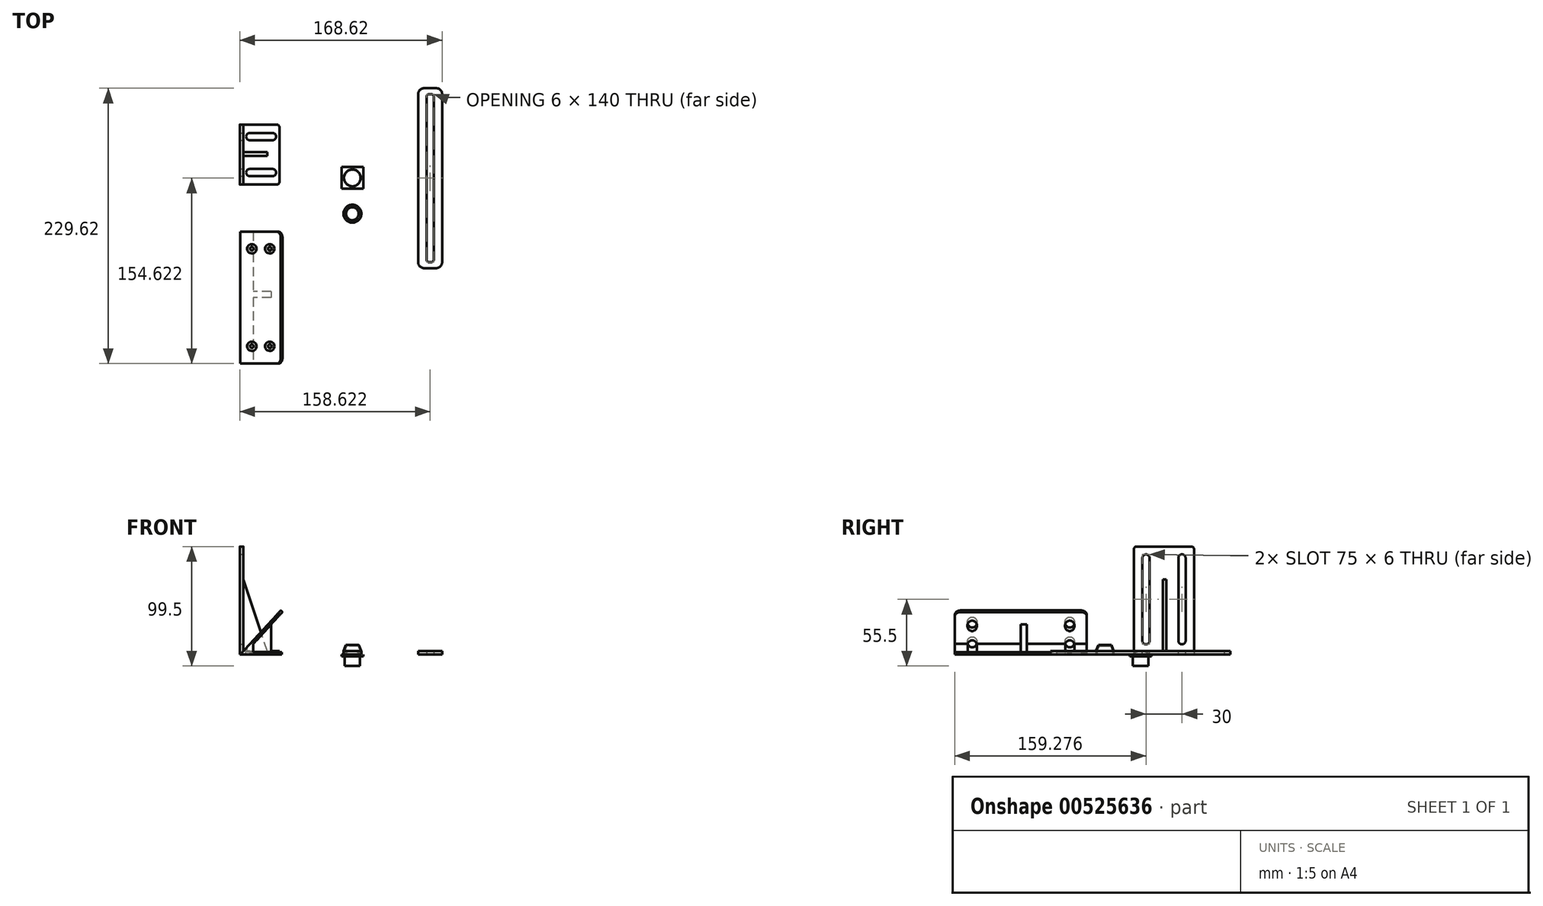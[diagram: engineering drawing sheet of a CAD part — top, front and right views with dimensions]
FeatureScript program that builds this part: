
annotation { "Feature Type Name" : "Feature", "Feature Type Description" : "" }
export const myFeature = defineFeature(function(context is Context, id is Id, definition is map)
    precondition{}
    {
        {
            var Q0;
            Q0=qCreatedBy(makeId("Top.planeOp"),FACE);
            var sketch = newSketch(context, id + "F0", { "sketchPlane" : qUnion([Q0])});
            skCircle(sketch, "E0", {"center": v(0, 0) * mm, "radius": 7 * mm});
            skSolve(sketch);
        }
        {
            var Q0;
            Q0=makeQuery(id+"F0.imprint","IMPRINT",FACE,{"disambiguationData":[TD([[makeQuery(id+"F0.imprint","IMPRINT",EDGE,{"derivedFrom":sQuery(id+"F0.wireOp",EDGE,"E0")}),1.0]])]});
            extrude(context, id + "F1", {"entities" : qUnion([Q0]), "depth" : 2.5 * mm, "offsetDistance" : 25 * mm});
        }
        {
            var Q0;
            Q0=makeQuery(id+"F1.opExtrude","CAP_EDGE",EDGE,{"disambiguationData":[OSD([sQuery(id+"F0.wireOp",EDGE,"E0")])],"isStart":false});
            fillet(context, id + "F2", {"entities" : qUnion([Q0]), "radius" : 7 * mm, "tangentPropagation" : true, "allowEdgeOverflow" : false});
        }
        {
            var Q0;
            Q0=makeQuery(id+"F1.opExtrude","CAP_FACE",FACE,{"disambiguationData":[OSD([sQuery(id+"F0.wireOp",EDGE,"E0")])],"isStart":true});
            cPlane(context, id + "F3", {"entities" : qUnion([Q0]), "cplaneType" : CPlaneType.OFFSET, "offset" : 0 * mm, "width" : 150 * mm, "height" : 150 * mm});
        }
        {
            var Q0;
            Q0=qCreatedBy(id+"F3.planeOp",FACE);
            var sketch = newSketch(context, id + "F4", { "sketchPlane" : qUnion([Q0])});
            skLineSegment(sketch, "E1.bottom", {"start": v(-9, -9) * mm, "end": v(9, -9) * mm});
            skLineSegment(sketch, "E1.top", {"start": v(-9, 9) * mm, "end": v(9, 9) * mm});
            skLineSegment(sketch, "E1.left", {"start": v(-9, -9) * mm, "end": v(-9, 9) * mm});
            skLineSegment(sketch, "E1.right", {"start": v(9, -9) * mm, "end": v(9, 9) * mm});
            skSolve(sketch);
        }
        {
            var Q0;
            Q0=qSketchRegion(id+"F4",true);
            extrude(context, id + "F5", {"entities" : qUnion([Q0]), "operationType" : NewBodyOperationType.ADD, "depth" : 1.5 * mm, "offsetDistance" : 25 * mm});
        }
        {
            var Q0;
            Q0=makeQuery(id+"F5.opExtrude","CAP_FACE",FACE,{"disambiguationData":[OSD([sQuery(id+"F4.wireOp",EDGE,"E1.bottom"),sQuery(id+"F4.wireOp",EDGE,"E1.top"),sQuery(id+"F4.wireOp",EDGE,"E1.left"),sQuery(id+"F4.wireOp",EDGE,"E1.right")])],"isStart":false});
            cPlane(context, id + "F6", {"entities" : qUnion([Q0]), "cplaneType" : CPlaneType.OFFSET, "offset" : 0 * mm, "width" : 150 * mm, "height" : 150 * mm});
        }
        {
            var Q0;
            Q0=qCreatedBy(id+"F6.planeOp",FACE);
            var sketch = newSketch(context, id + "F7", { "sketchPlane" : qUnion([Q0])});
            skCircle(sketch, "E2", {"center": v(0, 0) * mm, "radius": 6.4 * mm});
            skSolve(sketch);
        }
        {
            var Q0;
            Q0=qSketchRegion(id+"F7",true);
            extrude(context, id + "F8", {"entities" : qUnion([Q0]), "operationType" : NewBodyOperationType.ADD, "depth" : 8 * mm, "offsetDistance" : 25 * mm});
        }
        {
            var Q0;
            Q0=qCreatedBy(makeId("Top.planeOp"),FACE);
            var sketch = newSketch(context, id + "F9", { "sketchPlane" : qUnion([Q0])});
            skCircle(sketch, "E3", {"center": v(0, -29.84) * mm, "radius": 7.45 * mm});
            skSolve(sketch);
        }
        {
            var Q0;
            Q0=qSketchRegion(id+"F9",true);
            extrude(context, id + "F10", {"entities" : qUnion([Q0]), "depth" : 8 * mm, "offsetDistance" : 25 * mm});
        }
        {
            var Q0;
            Q0=makeQuery(id+"F10.opExtrude","CAP_EDGE",EDGE,{"disambiguationData":[OSD([sQuery(id+"F9.wireOp",EDGE,"E3")])],"isStart":false});
            chamfer(context, id + "F11", {"entities" : qUnion([Q0]), "chamferType" : ChamferType.TWO_OFFSETS, "width1" : 2 * mm, "oppositeDirection" : false, "width2" : 5 * mm, "tangentPropagation" : true});
        }
        {
            var Q0;
            Q0=qCreatedBy(makeId("Top.planeOp"),FACE);
            var sketch = newSketch(context, id + "F12", { "sketchPlane" : qUnion([Q0])});
            skCircle(sketch, "E4", {"center": v(0, -29.84) * mm, "radius": 6.45 * mm});
            skSolve(sketch);
        }
        {
            var Q0;
            Q0=qSketchRegion(id+"F12",true);
            extrude(context, id + "F13", {"entities" : qUnion([Q0]), "depth" : 7 * mm, "offsetDistance" : 25 * mm});
        }
        {
            var Q0;
            Q0=makeQuery(id+"F13.opExtrude","CAP_EDGE",EDGE,{"disambiguationData":[OSD([sQuery(id+"F12.wireOp",EDGE,"E4")])],"isStart":false});
            chamfer(context, id + "F14", {"entities" : qUnion([Q0]), "chamferType" : ChamferType.TWO_OFFSETS, "width1" : 1.7 * mm, "oppositeDirection" : false, "width2" : 4 * mm, "tangentPropagation" : true});
        }
        {
            var Q0;
            Q0=makeQuery(id+"F13.opExtrude","SWEPT_BODY",BODY,{"disambiguationData":[OSD([sQuery(id+"F12.wireOp",EDGE,"E4")])]});
            var Q1;
            Q1=makeQuery(id+"F10.opExtrude","SWEPT_BODY",BODY,{"disambiguationData":[OSD([sQuery(id+"F9.wireOp",EDGE,"E3")])]});
            booleanBodies(context, id + "F15", {"operationType" : BooleanOperationType.SUBTRACTION, "tools" : qUnion([Q0]), "targets" : qUnion([Q1])});
        }
        {
            var Q0;
            Q0=qCreatedBy(makeId("Top.planeOp"),FACE);
            var sketch = newSketch(context, id + "F16", { "sketchPlane" : qUnion([Q0])});
            skLineSegment(sketch, "E5.bottom", {"start": v(59.8, 74.78) * mm, "end": v(69.8, 74.78) * mm});
            skLineSegment(sketch, "E5.top", {"start": v(59.8, -75.22) * mm, "end": v(69.8, -75.22) * mm});
            skLineSegment(sketch, "E5.left", {"start": v(54.8, 69.78) * mm, "end": v(54.8, -70.22) * mm});
            skLineSegment(sketch, "E5.right", {"start": v(74.8, 69.78) * mm, "end": v(74.8, -70.22) * mm});
            skPoint(sketch, "E6.visualSharp", {"position": v(54.8, 74.78) * mm});
            skArc(sketch, "E6.filletArc", {"start": v(59.8, 74.78) * mm, "mid": v(56.27, 73.32) * mm, "end": v(54.8, 69.78) * mm});
            skPoint(sketch, "E7.visualSharp", {"position": v(74.8, 74.78) * mm});
            skArc(sketch, "E7.filletArc", {"start": v(74.8, 69.78) * mm, "mid": v(73.34, 73.32) * mm, "end": v(69.8, 74.78) * mm});
            skPoint(sketch, "E8.visualSharp", {"position": v(54.8, -75.22) * mm});
            skArc(sketch, "E8.filletArc", {"start": v(54.8, -70.22) * mm, "mid": v(56.27, -73.75) * mm, "end": v(59.8, -75.22) * mm});
            skPoint(sketch, "E9.visualSharp", {"position": v(74.8, -75.22) * mm});
            skArc(sketch, "E9.filletArc", {"start": v(69.8, -75.22) * mm, "mid": v(73.34, -73.75) * mm, "end": v(74.8, -70.22) * mm});
            skLineSegment(sketch, "E10.bottom", {"start": v(63.8, 69.78) * mm, "end": v(65.8, 69.78) * mm});
            skLineSegment(sketch, "E10.top", {"start": v(63.8, -70.22) * mm, "end": v(65.8, -70.22) * mm});
            skLineSegment(sketch, "E10.left", {"start": v(61.8, 67.78) * mm, "end": v(61.8, -68.22) * mm});
            skLineSegment(sketch, "E10.right", {"start": v(67.8, 67.78) * mm, "end": v(67.8, -68.22) * mm});
            skPoint(sketch, "E11.visualSharp", {"position": v(61.8, 69.78) * mm});
            skArc(sketch, "E11.filletArc", {"start": v(63.8, 69.78) * mm, "mid": v(62.39, 69.2) * mm, "end": v(61.8, 67.78) * mm});
            skPoint(sketch, "E12.visualSharp", {"position": v(61.8, -70.22) * mm});
            skArc(sketch, "E12.filletArc", {"start": v(61.8, -68.22) * mm, "mid": v(62.39, -69.63) * mm, "end": v(63.8, -70.22) * mm});
            skPoint(sketch, "E13.visualSharp", {"position": v(67.8, -70.22) * mm});
            skArc(sketch, "E13.filletArc", {"start": v(65.8, -70.22) * mm, "mid": v(67.22, -69.63) * mm, "end": v(67.8, -68.22) * mm});
            skPoint(sketch, "E14.visualSharp", {"position": v(67.8, 69.78) * mm});
            skArc(sketch, "E14.filletArc", {"start": v(67.8, 67.78) * mm, "mid": v(67.22, 69.2) * mm, "end": v(65.8, 69.78) * mm});
            skSolve(sketch);
        }
        {
            var Q0;
            Q0=qSketchRegion(id+"F16",true);
            extrude(context, id + "F17", {"entities" : qUnion([Q0]), "depth" : 3 * mm, "offsetDistance" : 25 * mm});
        }
        {
            var Q0;
            Q0=qCreatedBy(makeId("Top.planeOp"),FACE);
            var sketch = newSketch(context, id + "F18", { "sketchPlane" : qUnion([Q0])});
            skLineSegment(sketch, "E15.bottom", {"start": v(-90.82, 44.44) * mm, "end": v(-62.82, 44.44) * mm});
            skLineSegment(sketch, "E15.top", {"start": v(-90.82, -5.56) * mm, "end": v(-62.82, -5.56) * mm});
            skLineSegment(sketch, "E15.left", {"start": v(-90.82, 44.44) * mm, "end": v(-90.82, -5.56) * mm});
            skLineSegment(sketch, "E15.right", {"start": v(-60.82, 42.44) * mm, "end": v(-60.82, -3.56) * mm});
            skPoint(sketch, "E16.visualSharp", {"position": v(-60.82, 44.44) * mm});
            skArc(sketch, "E16.filletArc", {"start": v(-60.82, 42.44) * mm, "mid": v(-61.4, 43.85) * mm, "end": v(-62.82, 44.44) * mm});
            skPoint(sketch, "E17.visualSharp", {"position": v(-60.82, -5.56) * mm});
            skArc(sketch, "E17.filletArc", {"start": v(-62.82, -5.56) * mm, "mid": v(-61.4, -4.98) * mm, "end": v(-60.82, -3.56) * mm});
            skLineSegment(sketch, "E18.bottom", {"start": v(-101.44, 55.6) * mm, "end": v(-90.82, 55.6) * mm, "construction": true});
            skLineSegment(sketch, "E18.top", {"start": v(-101.44, -19.09) * mm, "end": v(-90.82, -19.09) * mm, "construction": true});
            skLineSegment(sketch, "E18.left", {"start": v(-101.44, 55.6) * mm, "end": v(-101.44, -19.09) * mm, "construction": true});
            skLineSegment(sketch, "E18.right", {"start": v(-90.82, 55.6) * mm, "end": v(-90.82, -19.09) * mm, "construction": true});
            skSolve(sketch);
        }
        {
            var Q0;
            Q0=qSketchRegion(id+"F18",true);
            extrude(context, id + "F19", {"entities" : qUnion([Q0]), "depth" : 3 * mm, "offsetDistance" : 25 * mm});
        }
        {
            var Q0;
            Q0=qCreatedBy(makeId("Top.planeOp"),FACE);
            var sketch = newSketch(context, id + "F20", { "sketchPlane" : qUnion([Q0])});
            skLineSegment(sketch, "E19.bottom", {"start": v(-93.82, 44.44) * mm, "end": v(-90.82, 44.44) * mm});
            skLineSegment(sketch, "E19.top", {"start": v(-93.82, -5.56) * mm, "end": v(-90.82, -5.56) * mm});
            skLineSegment(sketch, "E19.left", {"start": v(-93.82, 44.44) * mm, "end": v(-93.82, -5.56) * mm});
            skLineSegment(sketch, "E19.right", {"start": v(-90.82, 44.44) * mm, "end": v(-90.82, -5.56) * mm});
            skSolve(sketch);
        }
        {
            var Q0;
            Q0=qSketchRegion(id+"F20",true);
            extrude(context, id + "F21", {"entities" : qUnion([Q0]), "operationType" : NewBodyOperationType.ADD, "depth" : 90 * mm, "offsetDistance" : 25 * mm});
        }
        {
            var Q0;
            Q0=makeQuery(id+"F21.opExtrude","CAP_EDGE",EDGE,{"disambiguationData":[OSD([sQuery(id+"F20.wireOp",EDGE,"E19.top")])],"isStart":false});
            var Q1;
            Q1=makeQuery(id+"F21.opExtrude","CAP_EDGE",EDGE,{"disambiguationData":[OSD([sQuery(id+"F20.wireOp",EDGE,"E19.bottom")])],"isStart":false});
            fillet(context, id + "F22", {"entities" : qUnion([Q0, Q1]), "radius" : 2 * mm, "tangentPropagation" : true, "allowEdgeOverflow" : false});
        }
        {
            var Q0;
            Q0=makeQuery(id+"F19.opExtrude","CAP_FACE",FACE,{"disambiguationData":[OSD([sQuery(id+"F18.wireOp",EDGE,"E15.bottom"),sQuery(id+"F18.wireOp",EDGE,"E15.top"),sQuery(id+"F18.wireOp",EDGE,"E15.left"),sQuery(id+"F18.wireOp",EDGE,"E15.right"),sQuery(id+"F18.wireOp",EDGE,"E16.filletArc"),sQuery(id+"F18.wireOp",EDGE,"E17.filletArc")])],"isStart":false});
            var sketch = newSketch(context, id + "F23", { "sketchPlane" : qUnion([Q0])});
            skLineSegment(sketch, "E20.bottom", {"start": v(-85.49, 37.44) * mm, "end": v(-66.49, 37.44) * mm});
            skLineSegment(sketch, "E20.top", {"start": v(-85.49, 31.44) * mm, "end": v(-66.49, 31.44) * mm});
            skLineSegment(sketch, "E20.left", {"start": v(-88.49, 34.44) * mm, "end": v(-88.49, 34.44) * mm});
            skLineSegment(sketch, "E20.right", {"start": v(-63.49, 34.44) * mm, "end": v(-63.49, 34.44) * mm});
            skPoint(sketch, "E21.visualSharp", {"position": v(-88.49, 37.44) * mm});
            skArc(sketch, "E21.filletArc", {"start": v(-85.49, 37.44) * mm, "mid": v(-87.6, 36.56) * mm, "end": v(-88.49, 34.44) * mm});
            skPoint(sketch, "E22.visualSharp", {"position": v(-88.49, 31.44) * mm});
            skArc(sketch, "E22.filletArc", {"start": v(-88.49, 34.44) * mm, "mid": v(-87.6, 32.31) * mm, "end": v(-85.49, 31.44) * mm});
            skPoint(sketch, "E23.visualSharp", {"position": v(-63.49, 31.44) * mm});
            skArc(sketch, "E23.filletArc", {"start": v(-66.49, 31.44) * mm, "mid": v(-64.37, 32.31) * mm, "end": v(-63.49, 34.44) * mm});
            skPoint(sketch, "E24.visualSharp", {"position": v(-63.49, 37.44) * mm});
            skArc(sketch, "E24.filletArc", {"start": v(-63.49, 34.44) * mm, "mid": v(-64.37, 36.56) * mm, "end": v(-66.49, 37.44) * mm});
            skLineSegment(sketch, "E25.bottom", {"start": v(-85.49, 7.44) * mm, "end": v(-66.49, 7.44) * mm});
            skLineSegment(sketch, "E25.top", {"start": v(-85.49, 1.44) * mm, "end": v(-66.49, 1.44) * mm});
            skLineSegment(sketch, "E25.left", {"start": v(-88.49, 4.44) * mm, "end": v(-88.49, 4.44) * mm});
            skLineSegment(sketch, "E25.right", {"start": v(-63.49, 4.44) * mm, "end": v(-63.49, 4.44) * mm});
            skPoint(sketch, "E26.visualSharp", {"position": v(-88.49, 7.44) * mm});
            skArc(sketch, "E26.filletArc", {"start": v(-85.49, 7.44) * mm, "mid": v(-87.61, 6.56) * mm, "end": v(-88.49, 4.44) * mm});
            skPoint(sketch, "E27.visualSharp", {"position": v(-88.49, 1.44) * mm});
            skArc(sketch, "E27.filletArc", {"start": v(-88.49, 4.44) * mm, "mid": v(-87.61, 2.31) * mm, "end": v(-85.49, 1.44) * mm});
            skPoint(sketch, "E28.visualSharp", {"position": v(-63.49, 1.44) * mm});
            skArc(sketch, "E28.filletArc", {"start": v(-66.49, 1.44) * mm, "mid": v(-64.37, 2.31) * mm, "end": v(-63.49, 4.44) * mm});
            skPoint(sketch, "E29.visualSharp", {"position": v(-63.49, 7.44) * mm});
            skArc(sketch, "E29.filletArc", {"start": v(-63.49, 4.44) * mm, "mid": v(-64.37, 6.56) * mm, "end": v(-66.49, 7.44) * mm});
            skSolve(sketch);
        }
        {
            var Q0;
            Q0=qSketchRegion(id+"F23",true);
            extrude(context, id + "F24", {"entities" : qUnion([Q0]), "operationType" : NewBodyOperationType.REMOVE, "oppositeDirection" : true, "depth" : 25 * mm, "offsetDistance" : 25 * mm});
        }
        {
            var Q0;
            Q0=makeQuery(id+"F21.opExtrude","SWEPT_FACE",FACE,{"disambiguationData":[OSD([sQuery(id+"F20.wireOp",EDGE,"E19.right")])]});
            var sketch = newSketch(context, id + "F25", { "sketchPlane" : qUnion([Q0])});
            skLineSegment(sketch, "E30.bottom", {"start": v(34.44, 83.5) * mm, "end": v(34.44, 83.5) * mm});
            skLineSegment(sketch, "E30.top", {"start": v(34.44, 8.5) * mm, "end": v(34.44, 8.5) * mm});
            skLineSegment(sketch, "E30.left", {"start": v(31.44, 80.5) * mm, "end": v(31.44, 11.5) * mm});
            skLineSegment(sketch, "E30.right", {"start": v(37.44, 80.5) * mm, "end": v(37.44, 11.5) * mm});
            skPoint(sketch, "E31.visualSharp", {"position": v(31.44, 83.5) * mm});
            skArc(sketch, "E31.filletArc", {"start": v(34.44, 83.5) * mm, "mid": v(32.31, 82.62) * mm, "end": v(31.44, 80.5) * mm});
            skPoint(sketch, "E32.visualSharp", {"position": v(31.44, 8.5) * mm});
            skArc(sketch, "E32.filletArc", {"start": v(31.44, 11.5) * mm, "mid": v(32.31, 9.38) * mm, "end": v(34.44, 8.5) * mm});
            skPoint(sketch, "E33.visualSharp", {"position": v(37.44, 83.5) * mm});
            skArc(sketch, "E33.filletArc", {"start": v(37.44, 80.5) * mm, "mid": v(36.56, 82.62) * mm, "end": v(34.44, 83.5) * mm});
            skPoint(sketch, "E34.visualSharp", {"position": v(37.44, 8.5) * mm});
            skArc(sketch, "E34.filletArc", {"start": v(34.44, 8.5) * mm, "mid": v(36.56, 9.38) * mm, "end": v(37.44, 11.5) * mm});
            skLineSegment(sketch, "E35.bottom", {"start": v(49.07, 61.34) * mm, "end": v(49.07, 61.34) * mm});
            skLineSegment(sketch, "E35.top", {"start": v(49.07, -13.66) * mm, "end": v(49.07, -13.66) * mm});
            skLineSegment(sketch, "E35.left", {"start": v(1.44, 80.5) * mm, "end": v(1.44, 11.5) * mm});
            skLineSegment(sketch, "E35.right", {"start": v(7.44, 80.5) * mm, "end": v(7.44, 11.5) * mm});
            skPoint(sketch, "E36.visualSharp", {"position": v(1.44, 83.5) * mm});
            skArc(sketch, "E36.filletArc", {"start": v(4.44, 83.5) * mm, "mid": v(2.31, 82.62) * mm, "end": v(1.44, 80.5) * mm});
            skPoint(sketch, "E37.visualSharp", {"position": v(1.44, 8.5) * mm});
            skArc(sketch, "E37.filletArc", {"start": v(1.44, 11.5) * mm, "mid": v(2.31, 9.38) * mm, "end": v(4.44, 8.5) * mm});
            skPoint(sketch, "E38.visualSharp", {"position": v(7.44, 83.5) * mm});
            skArc(sketch, "E38.filletArc", {"start": v(7.44, 80.5) * mm, "mid": v(6.56, 82.62) * mm, "end": v(4.44, 83.5) * mm});
            skPoint(sketch, "E39.visualSharp", {"position": v(7.44, 8.5) * mm});
            skArc(sketch, "E39.filletArc", {"start": v(4.44, 8.5) * mm, "mid": v(6.56, 9.38) * mm, "end": v(7.44, 11.5) * mm});
            skSolve(sketch);
        }
        {
            var Q0;
            Q0=qSketchRegion(id+"F25",true);
            extrude(context, id + "F26", {"entities" : qUnion([Q0]), "operationType" : NewBodyOperationType.REMOVE, "oppositeDirection" : true, "depth" : 25 * mm, "offsetDistance" : 25 * mm});
        }
        {
            var Q0;
            Q0=makeQuery(id+"F29.boolean.opBoolean","MERGE",FACE,{"derivedFrom":[makeQuery(id+"F21.boolean.opBoolean","MERGE",FACE,{"derivedFrom":[makeQuery(id+"F19.opExtrude","SWEPT_FACE",FACE,{"disambiguationData":[OSD([sQuery(id+"F18.wireOp",EDGE,"E15.top")])]}),makeQuery(id+"F21.opExtrude","SWEPT_FACE",FACE,{"disambiguationData":[OSD([sQuery(id+"F20.wireOp",EDGE,"E19.top")])]})]}),makeQuery(id+"F29.opExtrude","CAP_FACE",FACE,{"disambiguationData":[OSD([sQuery(id+"F28.wireOp",EDGE,"E40"),sQuery(id+"F28.wireOp",EDGE,"E41"),sQuery(id+"F28.wireOp",EDGE,"E42")])],"isStart":true})]});
            cPlane(context, id + "F27", {"entities" : qUnion([Q0]), "cplaneType" : CPlaneType.OFFSET, "offset" : 24 * mm, "oppositeDirection" : true, "width" : 150 * mm, "height" : 150 * mm});
        }
        {
            var Q0;
            Q0=qCreatedBy(id+"F27.planeOp",FACE);
            var sketch = newSketch(context, id + "F28", { "sketchPlane" : qUnion([Q0])});
            skLineSegment(sketch, "E40", {"start": v(-90.82, 62.64) * mm, "end": v(-90.82, 3) * mm});
            skLineSegment(sketch, "E41", {"start": v(-90.82, 3) * mm, "end": v(-70.95, 3) * mm});
            skLineSegment(sketch, "E42", {"start": v(-70.95, 3) * mm, "end": v(-90.82, 62.64) * mm});
            skSolve(sketch);
        }
        {
            var Q0;
            Q0=makeQuery(id+"F28.imprint","IMPRINT",FACE,{"disambiguationData":[TD([[makeQuery(id+"F28.imprint","IMPRINT",EDGE,{"derivedFrom":sQuery(id+"F28.wireOp",EDGE,"E40")}),1.0]])]});
            extrude(context, id + "F29", {"entities" : qUnion([Q0]), "operationType" : NewBodyOperationType.ADD, "oppositeDirection" : true, "depth" : 3 * mm, "offsetDistance" : 25 * mm});
        }
        {
            var Q0;
            Q0=qCreatedBy(makeId("Top.planeOp"),FACE);
            var sketch = newSketch(context, id + "F30", { "sketchPlane" : qUnion([Q0])});
            skLineSegment(sketch, "E43.bottom", {"start": v(-88.77, -44.84) * mm, "end": v(-63.77, -44.84) * mm});
            skLineSegment(sketch, "E43.top", {"start": v(-88.77, -154.84) * mm, "end": v(-63.77, -154.84) * mm});
            skLineSegment(sketch, "E43.left", {"start": v(-88.77, -44.84) * mm, "end": v(-88.77, -154.84) * mm});
            skLineSegment(sketch, "E43.right", {"start": v(-58.77, -49.84) * mm, "end": v(-58.77, -149.84) * mm});
            skPoint(sketch, "E44.visualSharp", {"position": v(-58.77, -44.84) * mm});
            skArc(sketch, "E44.filletArc", {"start": v(-58.77, -49.84) * mm, "mid": v(-60.23, -46.3) * mm, "end": v(-63.77, -44.84) * mm});
            skPoint(sketch, "E45.visualSharp", {"position": v(-58.77, -154.84) * mm});
            skArc(sketch, "E45.filletArc", {"start": v(-63.77, -154.84) * mm, "mid": v(-60.23, -153.38) * mm, "end": v(-58.77, -149.84) * mm});
            skSolve(sketch);
        }
        {
            var Q0;
            Q0=qSketchRegion(id+"F30",true);
            extrude(context, id + "F31", {"entities" : qUnion([Q0]), "depth" : 2 * mm, "offsetDistance" : 25 * mm});
        }
        {
            var Q0;
            Q0=makeQuery(id+"F31.opExtrude","SWEPT_FACE",FACE,{"disambiguationData":[OSD([sQuery(id+"F30.wireOp",EDGE,"E43.top")])]});
            var sketch = newSketch(context, id + "F32", { "sketchPlane" : qUnion([Q0])});
            skLineSegment(sketch, "E46", {"start": v(-88.77, 2) * mm, "end": v(-58.2, 35.45) * mm});
            skLineSegment(sketch, "E47", {"start": v(-58.2, 35.45) * mm, "end": v(-59.67, 36.8) * mm});
            skLineSegment(sketch, "E48", {"start": v(-59.67, 36.8) * mm, "end": v(-93.3, 0) * mm});
            skLineSegment(sketch, "E49", {"start": v(-93.3, 0) * mm, "end": v(-88.77, 0) * mm});
            skLineSegment(sketch, "E50", {"start": v(-88.77, 0) * mm, "end": v(-88.77, 2) * mm});
            skSolve(sketch);
        }
        {
            var Q0;
            Q0=qSketchRegion(id+"F32",true);
            extrude(context, id + "F33", {"entities" : qUnion([Q0]), "operationType" : NewBodyOperationType.ADD, "oppositeDirection" : true, "depth" : 110 * mm, "offsetDistance" : 25 * mm});
        }
        {
            var Q0;
            Q0=makeQuery(id+"F33.opExtrude","CAP_EDGE",EDGE,{"disambiguationData":[OSD([sQuery(id+"F32.wireOp",EDGE,"E47")])],"isStart":true});
            var Q1;
            Q1=makeQuery(id+"F33.opExtrude","CAP_EDGE",EDGE,{"disambiguationData":[OSD([sQuery(id+"F32.wireOp",EDGE,"E47")])],"isStart":false});
            fillet(context, id + "F34", {"entities" : qUnion([Q0, Q1]), "radius" : 5 * mm, "tangentPropagation" : true, "allowEdgeOverflow" : false});
        }
        {
            var Q0;
            Q0=makeQuery(id+"F33.boolean.opBoolean","MERGE",FACE,{"derivedFrom":[makeQuery(id+"F31.opExtrude","SWEPT_FACE",FACE,{"disambiguationData":[OSD([sQuery(id+"F30.wireOp",EDGE,"E43.top")])]}),makeQuery(id+"F33.opExtrude","CAP_FACE",FACE,{"disambiguationData":[OSD([sQuery(id+"F32.wireOp",EDGE,"E46"),sQuery(id+"F32.wireOp",EDGE,"E47"),sQuery(id+"F32.wireOp",EDGE,"E48"),sQuery(id+"F32.wireOp",EDGE,"E49"),sQuery(id+"F32.wireOp",EDGE,"E50")])],"isStart":true})]});
            var sketch = newSketch(context, id + "F35", { "sketchPlane" : qUnion([Q0])});
            skLineSegment(sketch, "E51", {"start": v(-88.77, 2) * mm, "end": v(-82.5, 8.86) * mm});
            skLineSegment(sketch, "E52", {"start": v(-82.5, 8.86) * mm, "end": v(-82.5, 2) * mm});
            skLineSegment(sketch, "E53", {"start": v(-82.5, 2) * mm, "end": v(-88.77, 2) * mm});
            skSolve(sketch);
        }
        {
            var Q0;
            Q0=qSketchRegion(id+"F35",true);
            extrude(context, id + "F36", {"entities" : qUnion([Q0]), "operationType" : NewBodyOperationType.ADD, "oppositeDirection" : true, "depth" : 110 * mm, "offsetDistance" : 25 * mm});
        }
        {
            var Q0;
            Q0=qCreatedBy(makeId("Top.planeOp"),FACE);
            cPlane(context, id + "F37", {"entities" : qUnion([Q0]), "cplaneType" : CPlaneType.OFFSET, "offset" : 50 * mm, "width" : 150 * mm, "height" : 150 * mm});
        }
        {
            var Q0;
            Q0=qCreatedBy(id+"F37.planeOp",FACE);
            var sketch = newSketch(context, id + "F38", { "sketchPlane" : qUnion([Q0])});
            skPoint(sketch, "E54", {"position": v(-68.77, -59.07) * mm});
            skPoint(sketch, "E55", {"position": v(-83.77, -59.07) * mm});
            skPoint(sketch, "E56", {"position": v(-68.77, -140.34) * mm});
            skPoint(sketch, "E57", {"position": v(-83.77, -140.34) * mm});
            skSolve(sketch);
        }
        {
            var Q0;
            Q0=sQuery(id+"F38.wireOp",VERTEX,"E57");
            var Q1;
            Q1=sQuery(id+"F38.wireOp",VERTEX,"E56");
            var Q2;
            Q2=sQuery(id+"F38.wireOp",VERTEX,"E55");
            var Q3;
            Q3=sQuery(id+"F38.wireOp",VERTEX,"E54");
            var Q4;
            Q4=makeQuery(id+"F31.opExtrude","SWEPT_BODY",BODY,{"disambiguationData":[OSD([sQuery(id+"F30.wireOp",EDGE,"E43.bottom"),sQuery(id+"F30.wireOp",EDGE,"E43.top"),sQuery(id+"F30.wireOp",EDGE,"E43.left"),sQuery(id+"F30.wireOp",EDGE,"E43.right"),sQuery(id+"F30.wireOp",EDGE,"E44.filletArc"),sQuery(id+"F30.wireOp",EDGE,"E45.filletArc")])]});
            hole(context, id + "F39", {"style" : HoleStyle.SIMPLE, "endStyle" : HoleEndStyle.BLIND, "holeDiameter" : 3 * mm, "holeDepth" : 50 * mm, "tappedDepth" : 12 * mm, "tapClearance" : 3, "locations" : qUnion([Q0, Q1, Q2, Q3]), "scope" : qUnion([Q4])});
        }
        {
            var Q0;
            Q0=qCreatedBy(id+"F37.planeOp",FACE);
            var sketch = newSketch(context, id + "F40", { "sketchPlane" : qUnion([Q0])});
            skPoint(sketch, "E58", {"position": v(-68.77, -59.07) * mm});
            skPoint(sketch, "E59", {"position": v(-83.77, -59.07) * mm});
            skPoint(sketch, "E60", {"position": v(-68.77, -140.34) * mm});
            skPoint(sketch, "E61", {"position": v(-83.77, -140.34) * mm});
            skSolve(sketch);
        }
        {
            var Q0;
            Q0=sQuery(id+"F40.wireOp",VERTEX,"E61");
            var Q1;
            Q1=sQuery(id+"F40.wireOp",VERTEX,"E60");
            var Q2;
            Q2=sQuery(id+"F40.wireOp",VERTEX,"E58");
            var Q3;
            Q3=sQuery(id+"F40.wireOp",VERTEX,"E59");
            var Q4;
            Q4=makeQuery(id+"F31.opExtrude","SWEPT_BODY",BODY,{"disambiguationData":[OSD([sQuery(id+"F30.wireOp",EDGE,"E43.bottom"),sQuery(id+"F30.wireOp",EDGE,"E43.top"),sQuery(id+"F30.wireOp",EDGE,"E43.left"),sQuery(id+"F30.wireOp",EDGE,"E43.right"),sQuery(id+"F30.wireOp",EDGE,"E44.filletArc"),sQuery(id+"F30.wireOp",EDGE,"E45.filletArc")])]});
            hole(context, id + "F41", {"style" : HoleStyle.SIMPLE, "endStyle" : HoleEndStyle.BLIND, "holeDiameter" : 8 * mm, "holeDepth" : 19 * mm, "tappedDepth" : 12 * mm, "tapClearance" : 3, "locations" : qUnion([Q0, Q1, Q2, Q3]), "scope" : qUnion([Q4])});
        }
        {
            var Q0;
            Q0=makeQuery(id+"F33.boolean.opBoolean","MERGE",FACE,{"derivedFrom":[makeQuery(id+"F31.opExtrude","CAP_FACE",FACE,{"disambiguationData":[OSD([sQuery(id+"F30.wireOp",EDGE,"E43.bottom"),sQuery(id+"F30.wireOp",EDGE,"E43.top"),sQuery(id+"F30.wireOp",EDGE,"E43.left"),sQuery(id+"F30.wireOp",EDGE,"E43.right"),sQuery(id+"F30.wireOp",EDGE,"E44.filletArc"),sQuery(id+"F30.wireOp",EDGE,"E45.filletArc")])],"isStart":true}),makeQuery(id+"F33.opExtrude","SWEPT_FACE",FACE,{"disambiguationData":[OSD([sQuery(id+"F32.wireOp",EDGE,"E49")])]})]});
            var sketch = newSketch(context, id + "F42", { "sketchPlane" : qUnion([Q0])});
            skCircle(sketch, "E62", {"center": v(-83.77, 59.07) * mm, "radius": 4 * mm});
            skCircle(sketch, "E63", {"center": v(-83.77, 140.34) * mm, "radius": 4 * mm});
            skSolve(sketch);
        }
        {
            var Q0;
            Q0=qSketchRegion(id+"F42",true);
            extrude(context, id + "F43", {"entities" : qUnion([Q0]), "operationType" : NewBodyOperationType.ADD, "oppositeDirection" : true, "depth" : 2 * mm, "offsetDistance" : 25 * mm});
        }
        {
            var Q0;
            Q0=makeQuery(id+"F43.boolean.opBoolean","MERGE",FACE,{"derivedFrom":[makeQuery(id+"F31.opExtrude","CAP_FACE",FACE,{"disambiguationData":[OSD([sQuery(id+"F30.wireOp",EDGE,"E43.bottom"),sQuery(id+"F30.wireOp",EDGE,"E43.top"),sQuery(id+"F30.wireOp",EDGE,"E43.left"),sQuery(id+"F30.wireOp",EDGE,"E43.right"),sQuery(id+"F30.wireOp",EDGE,"E44.filletArc"),sQuery(id+"F30.wireOp",EDGE,"E45.filletArc")])],"isStart":false}),makeQuery(id+"F43.opExtrude","CAP_FACE",FACE,{"disambiguationData":[OSD([sQuery(id+"F42.wireOp",EDGE,"E62")])],"isStart":false}),makeQuery(id+"F43.opExtrude","CAP_FACE",FACE,{"disambiguationData":[OSD([sQuery(id+"F42.wireOp",EDGE,"E63")])],"isStart":false})]});
            var sketch = newSketch(context, id + "F44", { "sketchPlane" : qUnion([Q0])});
            skPoint(sketch, "E64", {"position": v(-83.77, -59.07) * mm});
            skPoint(sketch, "E65", {"position": v(-83.77, -140.34) * mm});
            skSolve(sketch);
        }
        {
            var Q0;
            Q0=sQuery(id+"F44.wireOp",VERTEX,"E64");
            var Q1;
            Q1=sQuery(id+"F44.wireOp",VERTEX,"E65");
            var Q2;
            Q2=makeQuery(id+"F31.opExtrude","SWEPT_BODY",BODY,{"disambiguationData":[OSD([sQuery(id+"F30.wireOp",EDGE,"E43.bottom"),sQuery(id+"F30.wireOp",EDGE,"E43.top"),sQuery(id+"F30.wireOp",EDGE,"E43.left"),sQuery(id+"F30.wireOp",EDGE,"E43.right"),sQuery(id+"F30.wireOp",EDGE,"E44.filletArc"),sQuery(id+"F30.wireOp",EDGE,"E45.filletArc")])]});
            hole(context, id + "F45", {"style" : HoleStyle.SIMPLE, "endStyle" : HoleEndStyle.BLIND, "holeDiameter" : 3 * mm, "holeDepth" : 19 * mm, "tappedDepth" : 12 * mm, "tapClearance" : 3, "locations" : qUnion([Q0, Q1]), "scope" : qUnion([Q2])});
        }
        {
            var Q0;
            Q0=makeQuery(id+"F36.boolean.opBoolean","MERGE",FACE,{"derivedFrom":[makeQuery(id+"F33.boolean.opBoolean","MERGE",FACE,{"derivedFrom":[makeQuery(id+"F31.opExtrude","SWEPT_FACE",FACE,{"disambiguationData":[OSD([sQuery(id+"F30.wireOp",EDGE,"E43.top")])]}),makeQuery(id+"F33.opExtrude","CAP_FACE",FACE,{"disambiguationData":[OSD([sQuery(id+"F32.wireOp",EDGE,"E46"),sQuery(id+"F32.wireOp",EDGE,"E47"),sQuery(id+"F32.wireOp",EDGE,"E48"),sQuery(id+"F32.wireOp",EDGE,"E49"),sQuery(id+"F32.wireOp",EDGE,"E50")])],"isStart":true})]}),makeQuery(id+"F36.opExtrude","CAP_FACE",FACE,{"disambiguationData":[OSD([sQuery(id+"F35.wireOp",EDGE,"E51"),sQuery(id+"F35.wireOp",EDGE,"E52"),sQuery(id+"F35.wireOp",EDGE,"E53")])],"isStart":true})]});
            cPlane(context, id + "F46", {"entities" : qUnion([Q0]), "cplaneType" : CPlaneType.OFFSET, "offset" : 55 * mm, "oppositeDirection" : true, "width" : 150 * mm, "height" : 150 * mm});
        }
        {
            var Q0;
            Q0=qCreatedBy(id+"F46.planeOp",FACE);
            var sketch = newSketch(context, id + "F47", { "sketchPlane" : qUnion([Q0])});
            skLineSegment(sketch, "E66", {"start": v(-67.67, 2) * mm, "end": v(-82.5, 2) * mm});
            skLineSegment(sketch, "E67", {"start": v(-82.5, 2) * mm, "end": v(-82.5, 8.86) * mm});
            skLineSegment(sketch, "E68", {"start": v(-82.5, 8.86) * mm, "end": v(-67.67, 25.08) * mm});
            skLineSegment(sketch, "E69", {"start": v(-67.67, 25.08) * mm, "end": v(-67.67, 2) * mm});
            skSolve(sketch);
        }
        {
            var Q0;
            Q0=qSketchRegion(id+"F47",true);
            extrude(context, id + "F48", {"entities" : qUnion([Q0]), "operationType" : NewBodyOperationType.ADD, "oppositeDirection" : true, "depth" : 5 * mm, "offsetDistance" : 25 * mm});
        }
    });
